# Revit family: 399_SIBER_GRUPO_SF ECO
name_source: partatom
category: Equipos mecánicos
revit_build: Autodesk Revit 2017 (Build: 20160225_1515(x64)
units: mm (PartAtom-declared; Revit-internal decimal feet)

## family parameters
Compartido = No
Corte con vacíos al cargar = No
Cota de conector redondo = Diámetro de uso
Punto de cálculo de habitación = No
Se basa en plano de trabajo = Sí
Siempre vertical = No
Tipo de pieza = Normal

## types (1)
- 399_SIBER_GRUPO_SF ECO
    Conexión conductos = Ø 160 mm || Ø 125 mm || Ø 80 mm
    D100 = Ø laterales : 100 mm
    D125 = Ø extraccion : 125 mm
    D160 = Ø expulsion : 160 mm
    Dimensiones = 460 x 360 x 181 mm
    Dimensiones (imagen) = 399_SIBER_GRUPO_SF ECO.jpg
    Elevación por defecto = 0 mm  [stored 0 ft]
    Peso = 4 kg
    Página web fabricante = www.siberzone.es
    Voltaje = 230 V
    Índice de protección = 50 Hz

note: [stored X ft] marks values corroborated as IEEE doubles in the binary element streams (Revit-internal decimal feet)
